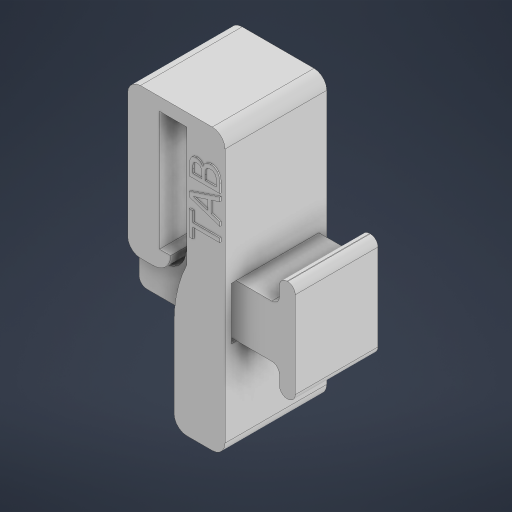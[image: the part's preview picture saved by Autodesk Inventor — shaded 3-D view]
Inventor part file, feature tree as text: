
AUTODESK INVENTOR PART (.ipt)
format: ipt  version: 2024.2 (Build 282272000, 272)  size: 386,048 bytes
history: native  units: in
note: dims shown in document units (in); Inventor stores cm internally (conversion verified against a paired STEP export)
features: extrude x6, fillet x4, thicken_offset x2, sketch x1
ambient origin geometry x8: Origin, YZ Plane, XZ Plane, XY Plane, X Axis, Y Axis, Z Axis, Center Point
bodies: Solid1 (feature_tree), Solid2 (feature_tree)
feature tree (13):
  sketch  "Sketch1"  dims[d0=0.215in d1=0.939in d2=0.027in d3=0.1in d4=0.8386in d5=0.25in d8=0.2306in d9=-0.0586in d10=0.25in d11=0.25in d12=0.1in d13=0.25in d14=0.3in d15=0.2in d16=0.4in d17=0.06in d18=0.0in d19=0.05in d20=0.0in d21=0.64in d22=0.0in d23=0.05in d24=0.0in d25=0.0669in d26=0.65in d27=0.0in d28=0.5in d29=0.01in d30=0.0in d31=0.002in d32=0.002in d33=0.002in d34=0.002in d35=1.0in d36=0.125in d37=0.8in d38=0.06in d39=0.06in d40=0.1in]
  extrude  "Extrusion1"  Depth=0.1in
  extrude  "Extrusion2"  Depth=0.1in
  extrude  "Extrusion3"  Depth=0.1in
  extrude  "Extrusion4"  Depth=0.1in
  extrude  "Extrusion5"  Depth=0.1in
  extrude  "Extrusion6"  Depth=0.1in
  thicken_offset  "Thicken1"
  thicken_offset  "Thicken2"
  fillet  "Fillet1"  [1 undecoded]
  fillet  "Fillet2"  Radius=0.25in
  fillet  "Fillet3"  Radius=0.25in
  fillet  "Fillet4"  Radius=0.1in
note: 1 required parameter value undecoded (feature->parameter linkage not recoverable at this tier; creation-order binding heuristic only, values carry confidence <= 0.55)
